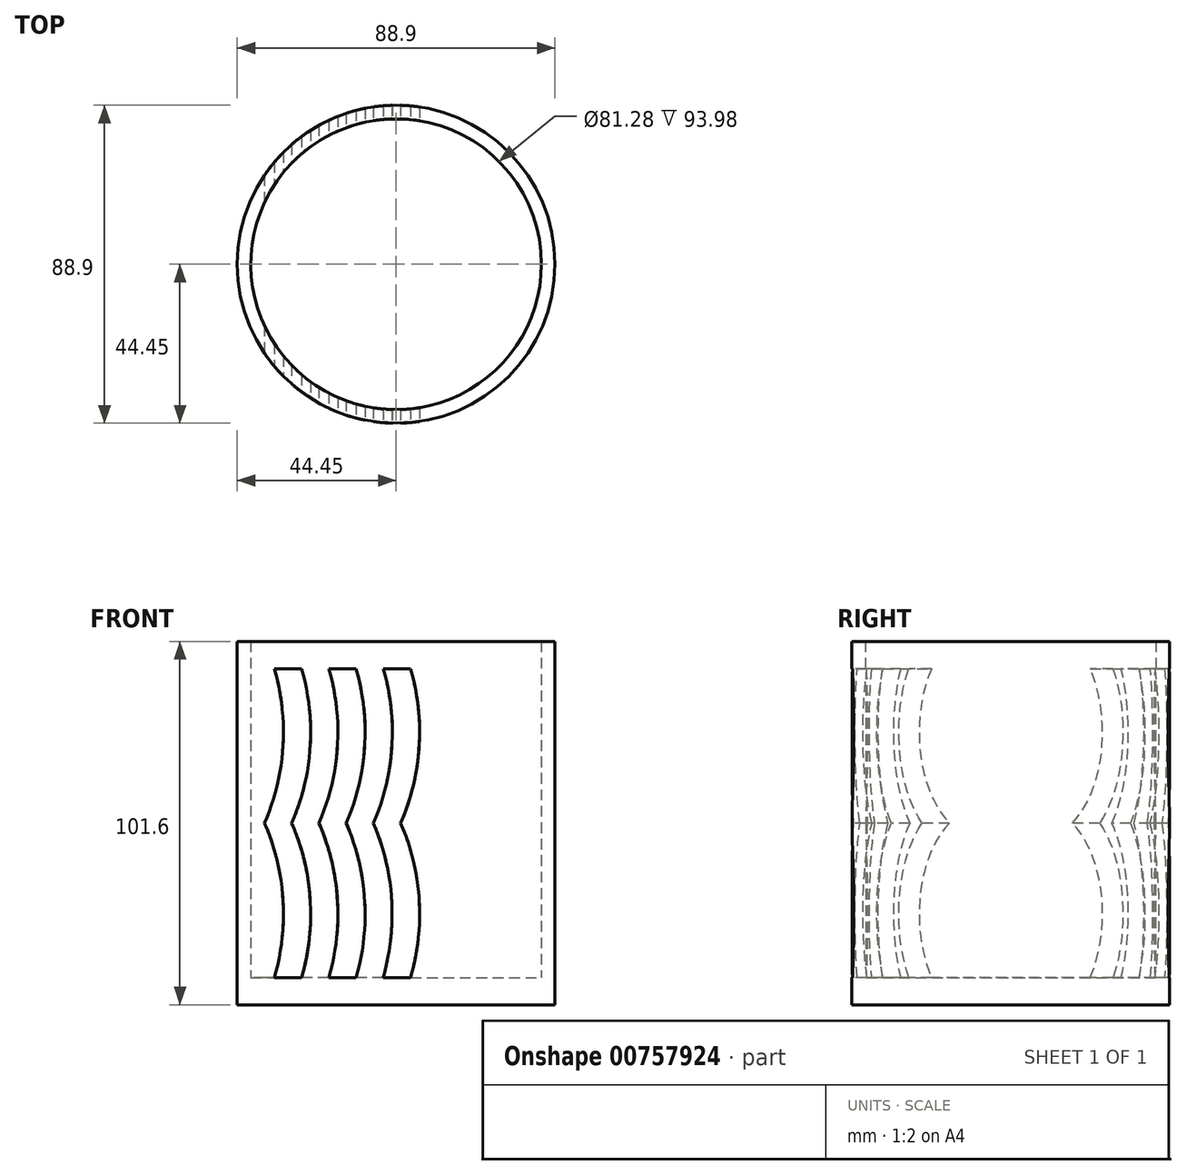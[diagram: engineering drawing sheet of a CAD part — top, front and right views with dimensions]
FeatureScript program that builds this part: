
annotation { "Feature Type Name" : "Feature", "Feature Type Description" : "" }
export const myFeature = defineFeature(function(context is Context, id is Id, definition is map)
    precondition{}
    {
        {
            var Q0;
            Q0=qCreatedBy(makeId("Top.planeOp"),FACE);
            var sketch = newSketch(context, id + "F0", { "sketchPlane" : qUnion([Q0])});
            skCircle(sketch, "E0", {"center": v(0, 0) * mm, "radius": 44.45 * mm});
            skCircle(sketch, "E1", {"center": v(0, 0) * mm, "radius": 40.64 * mm});
            skLineSegment(sketch, "E2.bottom", {"start": v(0, 0) * mm, "end": v(-44.45, 0) * mm});
            skLineSegment(sketch, "E2.top", {"start": v(0, 44.45) * mm, "end": v(-44.45, 44.45) * mm});
            skLineSegment(sketch, "E2.left", {"start": v(0, 0) * mm, "end": v(0, 44.45) * mm});
            skLineSegment(sketch, "E2.right", {"start": v(-44.45, 0) * mm, "end": v(-44.45, 44.45) * mm});
            skLineSegment(sketch, "E3.bottom", {"start": v(-44.45, 44.45) * mm, "end": v(44.45, 44.45) * mm});
            skLineSegment(sketch, "E3.top", {"start": v(-44.45, -44.45) * mm, "end": v(44.45, -44.45) * mm});
            skLineSegment(sketch, "E3.left", {"start": v(-44.45, 44.45) * mm, "end": v(-44.45, -44.45) * mm});
            skLineSegment(sketch, "E3.right", {"start": v(44.45, 44.45) * mm, "end": v(44.45, -44.45) * mm});
            skLineSegment(sketch, "E4.bottom", {"start": v(0, 0) * mm, "end": v(-40.64, 0) * mm});
            skLineSegment(sketch, "E4.top", {"start": v(0, 40.64) * mm, "end": v(-40.64, 40.64) * mm});
            skLineSegment(sketch, "E4.left", {"start": v(0, 0) * mm, "end": v(0, 40.64) * mm});
            skLineSegment(sketch, "E4.right", {"start": v(-40.64, 0) * mm, "end": v(-40.64, 40.64) * mm});
            skLineSegment(sketch, "E5.bottom", {"start": v(-40.64, 40.64) * mm, "end": v(40.64, 40.64) * mm});
            skLineSegment(sketch, "E5.top", {"start": v(-40.64, -40.64) * mm, "end": v(40.64, -40.64) * mm});
            skLineSegment(sketch, "E5.left", {"start": v(-40.64, 40.64) * mm, "end": v(-40.64, -40.64) * mm});
            skLineSegment(sketch, "E5.right", {"start": v(40.64, 40.64) * mm, "end": v(40.64, -40.64) * mm});
            skSolve(sketch);
        }
        {
            var Q0;
            {var subQ3=sQuery(id+"F0.wireOp",EDGE,"E1");var subQ5=makeQuery(id+"F0.imprint","INTERSECT",VERTEX,{"derivedFrom":[subQ3,sQuery(id+"F0.wireOp",EDGE,"E5.top")]});Q0=makeQuery(id+"F0.imprint","IMPRINT",FACE,{"disambiguationData":[TD([[makeQuery(id+"F0.imprint","IMPRINT",EDGE,{"disambiguationData":[TD([[subQ5,-1.0]])],"derivedFrom":subQ3}),1.0]])]});}
            var Q1;
            {var subQ0=sQuery(id+"F0.wireOp",EDGE,"E2.left");var subQ3=sQuery(id+"F0.wireOp",EDGE,"E2.bottom");var subQ5=makeQuery(id+"F0.imprint","INTERSECT",VERTEX,{"derivedFrom":[subQ3,subQ0]});Q1=makeQuery(id+"F0.imprint","IMPRINT",FACE,{"disambiguationData":[TD([[makeQuery(id+"F0.imprint","IMPRINT",EDGE,{"disambiguationData":[TD([[subQ5,-1.0]])],"derivedFrom":subQ3}),-1.0]])]});}
            extrude(context, id + "F1", {"entities" : qUnion([Q0, Q1]), "depth" : 7.62 * mm, "offsetDistance" : 25.4 * mm});
        }
        {
            var Q0;
            {var subQ4=sQuery(id+"F0.wireOp",EDGE,"E2.top");Q0=makeQuery(id+"F0.imprint","IMPRINT",FACE,{"disambiguationData":[TD([[makeQuery(id+"F0.imprint","IMPRINT",EDGE,{"derivedFrom":subQ4}),1.0]])]});}
            var Q1;
            {var subQ1=sQuery(id+"F0.wireOp",EDGE,"E0");var subQ3=sQuery(id+"F0.wireOp",EDGE,"E4.top");var subQ4=makeQuery(id+"F0.imprint","INTERSECT",VERTEX,{"derivedFrom":[subQ1,subQ3]});Q1=makeQuery(id+"F0.imprint","IMPRINT",FACE,{"disambiguationData":[TD([[makeQuery(id+"F0.imprint","IMPRINT",EDGE,{"disambiguationData":[TD([[subQ4,1.0]])],"derivedFrom":subQ1}),1.0]])]});}
            var Q2;
            {var subQ1=sQuery(id+"F0.wireOp",EDGE,"E0");var subQ3=sQuery(id+"F0.wireOp",EDGE,"E5.bottom");var subQ4=makeQuery(id+"F0.imprint","INTERSECT",VERTEX,{"derivedFrom":[subQ1,subQ3]});Q2=makeQuery(id+"F0.imprint","IMPRINT",FACE,{"disambiguationData":[TD([[makeQuery(id+"F0.imprint","IMPRINT",EDGE,{"disambiguationData":[TD([[subQ4,-1.0]])],"derivedFrom":subQ1}),1.0]])]});}
            var Q3;
            {var subQ1=sQuery(id+"F0.wireOp",EDGE,"E3.bottom");Q3=makeQuery(id+"F0.imprint","IMPRINT",FACE,{"disambiguationData":[TD([[makeQuery(id+"F0.imprint","IMPRINT",EDGE,{"derivedFrom":subQ1}),-1.0]])]});}
            var Q4;
            {var subQ0=sQuery(id+"F0.wireOp",EDGE,"E0");var subQ1=makeQuery(id+"F0.imprint","INTERSECT",VERTEX,{"derivedFrom":[subQ0,sQuery(id+"F0.wireOp",EDGE,"E3.right")]});Q4=makeQuery(id+"F0.imprint","IMPRINT",FACE,{"disambiguationData":[TD([[makeQuery(id+"F0.imprint","IMPRINT",EDGE,{"disambiguationData":[TD([[subQ1,-1.0]])],"derivedFrom":subQ0}),1.0]])]});}
            var Q5;
            {var subQ3=sQuery(id+"F0.wireOp",EDGE,"E0");var subQ8=sQuery(id+"F0.wireOp",EDGE,"E5.top");var subQ9=makeQuery(id+"F0.imprint","INTERSECT",VERTEX,{"disambiguationData":[OD(0.0)],"derivedFrom":[subQ3,subQ8]});Q5=makeQuery(id+"F0.imprint","IMPRINT",FACE,{"disambiguationData":[TD([[makeQuery(id+"F0.imprint","IMPRINT",EDGE,{"disambiguationData":[TD([[subQ9,1.0]])],"derivedFrom":subQ3}),-1.0]])]});}
            var Q6;
            {var subQ0=sQuery(id+"F0.wireOp",EDGE,"E0");var subQ1=makeQuery(id+"F0.imprint","INTERSECT",VERTEX,{"derivedFrom":[subQ0,sQuery(id+"F0.wireOp",EDGE,"E3.top")]});Q6=makeQuery(id+"F0.imprint","IMPRINT",FACE,{"disambiguationData":[TD([[makeQuery(id+"F0.imprint","IMPRINT",EDGE,{"disambiguationData":[TD([[subQ1,1.0]])],"derivedFrom":subQ0}),1.0]])]});}
            var Q7;
            {var subQ1=sQuery(id+"F0.wireOp",EDGE,"E0");var subQ3=sQuery(id+"F0.wireOp",EDGE,"E4.right");var subQ4=makeQuery(id+"F0.imprint","INTERSECT",VERTEX,{"derivedFrom":[subQ1,subQ3]});Q7=makeQuery(id+"F0.imprint","IMPRINT",FACE,{"disambiguationData":[TD([[makeQuery(id+"F0.imprint","IMPRINT",EDGE,{"disambiguationData":[TD([[subQ4,-1.0]])],"derivedFrom":subQ1}),1.0]])]});}
            var Q8;
            {var subQ1=sQuery(id+"F0.wireOp",EDGE,"E0");var subQ3=sQuery(id+"F0.wireOp",EDGE,"E5.left");var subQ4=makeQuery(id+"F0.imprint","INTERSECT",VERTEX,{"derivedFrom":[subQ1,subQ3]});Q8=makeQuery(id+"F0.imprint","IMPRINT",FACE,{"disambiguationData":[TD([[makeQuery(id+"F0.imprint","IMPRINT",EDGE,{"disambiguationData":[TD([[subQ4,1.0]])],"derivedFrom":subQ1}),1.0]])]});}
            var Q9;
            {var subQ0=sQuery(id+"F0.wireOp",EDGE,"E3.left");Q9=makeQuery(id+"F0.imprint","IMPRINT",FACE,{"disambiguationData":[TD([[makeQuery(id+"F0.imprint","IMPRINT",EDGE,{"derivedFrom":subQ0}),1.0]])]});}
            var Q10;
            {var subQ0=sQuery(id+"F0.wireOp",EDGE,"E4.top");var subQ1=sQuery(id+"F0.wireOp",EDGE,"E0");var subQ2=makeQuery(id+"F0.imprint","INTERSECT",VERTEX,{"derivedFrom":[subQ1,subQ0]});Q10=makeQuery(id+"F0.imprint","IMPRINT",FACE,{"disambiguationData":[TD([[makeQuery(id+"F0.imprint","IMPRINT",EDGE,{"disambiguationData":[TD([[subQ2,-1.0]])],"derivedFrom":subQ1}),-1.0]])]});}
            var Q11;
            {var subQ0=sQuery(id+"F0.wireOp",EDGE,"E5.bottom");var subQ1=sQuery(id+"F0.wireOp",EDGE,"E0");var subQ2=makeQuery(id+"F0.imprint","INTERSECT",VERTEX,{"derivedFrom":[subQ1,subQ0]});Q11=makeQuery(id+"F0.imprint","IMPRINT",FACE,{"disambiguationData":[TD([[makeQuery(id+"F0.imprint","IMPRINT",EDGE,{"disambiguationData":[TD([[subQ2,1.0]])],"derivedFrom":subQ1}),-1.0]])]});}
            var Q12;
            {var subQ0=sQuery(id+"F0.wireOp",EDGE,"E5.left");var subQ1=sQuery(id+"F0.wireOp",EDGE,"E0");var subQ2=makeQuery(id+"F0.imprint","INTERSECT",VERTEX,{"derivedFrom":[subQ1,subQ0]});Q12=makeQuery(id+"F0.imprint","IMPRINT",FACE,{"disambiguationData":[TD([[makeQuery(id+"F0.imprint","IMPRINT",EDGE,{"disambiguationData":[TD([[subQ2,-1.0]])],"derivedFrom":subQ1}),-1.0]])]});}
            var Q13;
            {var subQ0=sQuery(id+"F0.wireOp",EDGE,"E5.top");var subQ1=sQuery(id+"F0.wireOp",EDGE,"E0");var subQ2=makeQuery(id+"F0.imprint","INTERSECT",VERTEX,{"disambiguationData":[OD(0.0)],"derivedFrom":[subQ1,subQ0]});Q13=makeQuery(id+"F0.imprint","IMPRINT",FACE,{"disambiguationData":[TD([[makeQuery(id+"F0.imprint","IMPRINT",EDGE,{"disambiguationData":[TD([[subQ2,-1.0]])],"derivedFrom":subQ1}),-1.0]])]});}
            var Q14;
            {var subQ0=sQuery(id+"F0.wireOp",EDGE,"E5.bottom");var subQ1=sQuery(id+"F0.wireOp",EDGE,"E0");var subQ2=makeQuery(id+"F0.imprint","INTERSECT",VERTEX,{"derivedFrom":[subQ1,subQ0]});Q14=makeQuery(id+"F0.imprint","IMPRINT",FACE,{"disambiguationData":[TD([[makeQuery(id+"F0.imprint","IMPRINT",EDGE,{"disambiguationData":[TD([[subQ2,1.0]])],"derivedFrom":subQ1}),1.0]])]});}
            var Q15;
            {var subQ0=sQuery(id+"F0.wireOp",EDGE,"E4.top");var subQ1=sQuery(id+"F0.wireOp",EDGE,"E0");var subQ2=makeQuery(id+"F0.imprint","INTERSECT",VERTEX,{"derivedFrom":[subQ1,subQ0]});Q15=makeQuery(id+"F0.imprint","IMPRINT",FACE,{"disambiguationData":[TD([[makeQuery(id+"F0.imprint","IMPRINT",EDGE,{"disambiguationData":[TD([[subQ2,-1.0]])],"derivedFrom":subQ1}),1.0]])]});}
            var Q16;
            {var subQ0=sQuery(id+"F0.wireOp",EDGE,"E5.left");var subQ1=sQuery(id+"F0.wireOp",EDGE,"E0");var subQ2=makeQuery(id+"F0.imprint","INTERSECT",VERTEX,{"derivedFrom":[subQ1,subQ0]});Q16=makeQuery(id+"F0.imprint","IMPRINT",FACE,{"disambiguationData":[TD([[makeQuery(id+"F0.imprint","IMPRINT",EDGE,{"disambiguationData":[TD([[subQ2,-1.0]])],"derivedFrom":subQ1}),1.0]])]});}
            var Q17;
            {var subQ0=sQuery(id+"F0.wireOp",EDGE,"E5.top");var subQ1=sQuery(id+"F0.wireOp",EDGE,"E0");var subQ2=makeQuery(id+"F0.imprint","INTERSECT",VERTEX,{"disambiguationData":[OD(0.0)],"derivedFrom":[subQ1,subQ0]});Q17=makeQuery(id+"F0.imprint","IMPRINT",FACE,{"disambiguationData":[TD([[makeQuery(id+"F0.imprint","IMPRINT",EDGE,{"disambiguationData":[TD([[subQ2,-1.0]])],"derivedFrom":subQ1}),1.0]])]});}
            extrude(context, id + "F2", {"entities" : qUnion([Q0, Q1, Q2, Q3, Q4, Q5, Q6, Q7, Q8, Q9, Q10, Q11, Q12, Q13, Q14, Q15, Q16, Q17]), "operationType" : NewBodyOperationType.ADD, "depth" : 101.6 * mm, "offsetDistance" : 25.4 * mm});
        }
        {
            var Q0;
            Q0=makeQuery(id+"F2.opExtrude","SWEPT_FACE",FACE,{"disambiguationData":[OSD([sQuery(id+"F0.wireOp",EDGE,"E3.top")])]});
            var sketch = newSketch(context, id + "F3", { "sketchPlane" : qUnion([Q0])});
            skLineSegment(sketch, "E6", {"start": v(-44.45, 101.6) * mm, "end": v(-36.83, 101.6) * mm});
            skLineSegment(sketch, "E7", {"start": v(-36.83, 101.6) * mm, "end": v(-36.83, 0) * mm});
            skArc(sketch, "E8", {"start": v(-36.83, 50.8) * mm, "mid": v(-31.53, 76.2) * mm, "end": v(-36.83, 101.6) * mm});
            skArc(sketch, "E9", {"start": v(-36.83, 0) * mm, "mid": v(-31.53, 25.4) * mm, "end": v(-36.83, 50.8) * mm});
            skLineSegment(sketch, "E10", {"start": v(-36.83, 101.6) * mm, "end": v(-29.21, 101.6) * mm});
            skArc(sketch, "E11", {"start": v(-29.21, 50.8) * mm, "mid": v(-23.9, 76.2) * mm, "end": v(-29.21, 101.6) * mm});
            skArc(sketch, "E12", {"start": v(-29.21, 0) * mm, "mid": v(-23.9, 25.4) * mm, "end": v(-29.2, 50.8) * mm});
            skLineSegment(sketch, "E13", {"start": v(-29.21, 101.6) * mm, "end": v(-21.6, 101.6) * mm});
            skArc(sketch, "E14", {"start": v(-21.59, 50.8) * mm, "mid": v(-16.29, 76.2) * mm, "end": v(-21.59, 101.6) * mm});
            skArc(sketch, "E15", {"start": v(-21.6, 0) * mm, "mid": v(-16.29, 25.4) * mm, "end": v(-21.59, 50.8) * mm});
            skLineSegment(sketch, "E16", {"start": v(-21.6, 101.6) * mm, "end": v(-13.97, 101.6) * mm});
            skArc(sketch, "E17", {"start": v(-13.97, 50.8) * mm, "mid": v(-8.67, 76.2) * mm, "end": v(-13.97, 101.6) * mm});
            skArc(sketch, "E18", {"start": v(-13.97, 0) * mm, "mid": v(-8.67, 25.4) * mm, "end": v(-13.97, 50.8) * mm});
            skLineSegment(sketch, "E19", {"start": v(-44.45, 101.6) * mm, "end": v(-44.45, 93.98) * mm});
            skLineSegment(sketch, "E20", {"start": v(-44.45, 93.98) * mm, "end": v(44.45, 93.98) * mm});
            skLineSegment(sketch, "E21", {"start": v(-44.45, 0) * mm, "end": v(-44.45, 7.62) * mm});
            skLineSegment(sketch, "E22", {"start": v(-44.45, 7.62) * mm, "end": v(44.45, 7.62) * mm});
            skLineSegment(sketch, "E23", {"start": v(-13.97, 101.6) * mm, "end": v(-6.35, 101.6) * mm});
            skArc(sketch, "E24", {"start": v(-6.35, 50.8) * mm, "mid": v(-1.05, 76.2) * mm, "end": v(-6.35, 101.6) * mm});
            skArc(sketch, "E25", {"start": v(-6.35, 0) * mm, "mid": v(-1.13, 25.4) * mm, "end": v(-6.35, 50.8) * mm});
            skLineSegment(sketch, "E26", {"start": v(-6.35, 101.6) * mm, "end": v(1.27, 101.6) * mm});
            skArc(sketch, "E27", {"start": v(1.27, 50.8) * mm, "mid": v(6.57, 76.2) * mm, "end": v(1.27, 101.6) * mm});
            skArc(sketch, "E28", {"start": v(1.27, 0) * mm, "mid": v(6.57, 25.4) * mm, "end": v(1.27, 50.8) * mm});
            skSolve(sketch);
        }
        {
            var Q0;
            {var subQ0=sQuery(id+"F3.wireOp",EDGE,"E12");var subQ1=sQuery(id+"F3.wireOp",EDGE,"E11");var subQ2=makeQuery(id+"F3.imprint","INTERSECT",VERTEX,{"derivedFrom":[subQ1,subQ0]});Q0=makeQuery(id+"F3.imprint","IMPRINT",FACE,{"disambiguationData":[TD([[makeQuery(id+"F3.imprint","IMPRINT",EDGE,{"disambiguationData":[TD([[subQ2,-1.0]])],"derivedFrom":subQ1}),1.0]])]});}
            var Q1;
            {var subQ5=sQuery(id+"F3.wireOp",EDGE,"E15");var subQ6=sQuery(id+"F3.wireOp",EDGE,"E14");var subQ7=makeQuery(id+"F3.imprint","INTERSECT",VERTEX,{"derivedFrom":[subQ6,subQ5]});Q1=makeQuery(id+"F3.imprint","IMPRINT",FACE,{"disambiguationData":[TD([[makeQuery(id+"F3.imprint","IMPRINT",EDGE,{"disambiguationData":[TD([[subQ7,-1.0]])],"derivedFrom":subQ6}),-1.0]])]});}
            var Q2;
            {var subQ1=sQuery(id+"F3.wireOp",EDGE,"E24");var subQ3=sQuery(id+"F3.wireOp",EDGE,"E20");var subQ4=makeQuery(id+"F3.imprint","INTERSECT",VERTEX,{"derivedFrom":[subQ3,subQ1]});Q2=makeQuery(id+"F3.imprint","IMPRINT",FACE,{"disambiguationData":[TD([[makeQuery(id+"F3.imprint","IMPRINT",EDGE,{"disambiguationData":[TD([[subQ4,-1.0]])],"derivedFrom":subQ3}),-1.0]])]});}
            extrude(context, id + "F4", {"entities" : qUnion([Q0, Q1, Q2]), "operationType" : NewBodyOperationType.REMOVE, "endBound" : BoundingType.THROUGH_ALL, "oppositeDirection" : true, "depth" : 25.4 * mm, "offsetDistance" : 25.4 * mm});
        }
        {
            var Q0;
            {var subQ0=sQuery(id+"F0.wireOp",EDGE,"E3.left");Q0=makeQuery(id+"F0.imprint","IMPRINT",FACE,{"disambiguationData":[TD([[makeQuery(id+"F0.imprint","IMPRINT",EDGE,{"derivedFrom":subQ0}),1.0]])]});}
            var Q1;
            {var subQ0=sQuery(id+"F0.wireOp",EDGE,"E5.left");var subQ1=sQuery(id+"F0.wireOp",EDGE,"E0");var subQ2=makeQuery(id+"F0.imprint","INTERSECT",VERTEX,{"derivedFrom":[subQ1,subQ0]});Q1=makeQuery(id+"F0.imprint","IMPRINT",FACE,{"disambiguationData":[TD([[makeQuery(id+"F0.imprint","IMPRINT",EDGE,{"disambiguationData":[TD([[subQ2,-1.0]])],"derivedFrom":subQ1}),-1.0]])]});}
            var Q2;
            {var subQ0=sQuery(id+"F0.wireOp",EDGE,"E4.top");var subQ1=sQuery(id+"F0.wireOp",EDGE,"E0");var subQ2=makeQuery(id+"F0.imprint","INTERSECT",VERTEX,{"derivedFrom":[subQ1,subQ0]});Q2=makeQuery(id+"F0.imprint","IMPRINT",FACE,{"disambiguationData":[TD([[makeQuery(id+"F0.imprint","IMPRINT",EDGE,{"disambiguationData":[TD([[subQ2,-1.0]])],"derivedFrom":subQ1}),-1.0]])]});}
            var Q3;
            {var subQ4=sQuery(id+"F0.wireOp",EDGE,"E2.top");Q3=makeQuery(id+"F0.imprint","IMPRINT",FACE,{"disambiguationData":[TD([[makeQuery(id+"F0.imprint","IMPRINT",EDGE,{"derivedFrom":subQ4}),1.0]])]});}
            var Q4;
            {var subQ0=sQuery(id+"F0.wireOp",EDGE,"E5.bottom");var subQ1=sQuery(id+"F0.wireOp",EDGE,"E0");var subQ2=makeQuery(id+"F0.imprint","INTERSECT",VERTEX,{"derivedFrom":[subQ1,subQ0]});Q4=makeQuery(id+"F0.imprint","IMPRINT",FACE,{"disambiguationData":[TD([[makeQuery(id+"F0.imprint","IMPRINT",EDGE,{"disambiguationData":[TD([[subQ2,1.0]])],"derivedFrom":subQ1}),-1.0]])]});}
            var Q5;
            {var subQ1=sQuery(id+"F0.wireOp",EDGE,"E3.bottom");Q5=makeQuery(id+"F0.imprint","IMPRINT",FACE,{"disambiguationData":[TD([[makeQuery(id+"F0.imprint","IMPRINT",EDGE,{"derivedFrom":subQ1}),-1.0]])]});}
            var Q6;
            {var subQ0=sQuery(id+"F0.wireOp",EDGE,"E5.top");var subQ1=sQuery(id+"F0.wireOp",EDGE,"E0");var subQ2=makeQuery(id+"F0.imprint","INTERSECT",VERTEX,{"disambiguationData":[OD(0.0)],"derivedFrom":[subQ1,subQ0]});Q6=makeQuery(id+"F0.imprint","IMPRINT",FACE,{"disambiguationData":[TD([[makeQuery(id+"F0.imprint","IMPRINT",EDGE,{"disambiguationData":[TD([[subQ2,-1.0]])],"derivedFrom":subQ1}),-1.0]])]});}
            var Q7;
            {var subQ3=sQuery(id+"F0.wireOp",EDGE,"E0");var subQ8=sQuery(id+"F0.wireOp",EDGE,"E5.top");var subQ9=makeQuery(id+"F0.imprint","INTERSECT",VERTEX,{"disambiguationData":[OD(0.0)],"derivedFrom":[subQ3,subQ8]});Q7=makeQuery(id+"F0.imprint","IMPRINT",FACE,{"disambiguationData":[TD([[makeQuery(id+"F0.imprint","IMPRINT",EDGE,{"disambiguationData":[TD([[subQ9,1.0]])],"derivedFrom":subQ3}),-1.0]])]});}
            extrude(context, id + "F5", {"entities" : qUnion([Q0, Q1, Q2, Q3, Q4, Q5, Q6, Q7]), "operationType" : NewBodyOperationType.REMOVE, "endBound" : BoundingType.THROUGH_ALL, "depth" : 25.4 * mm, "offsetDistance" : 25.4 * mm});
        }
    });
